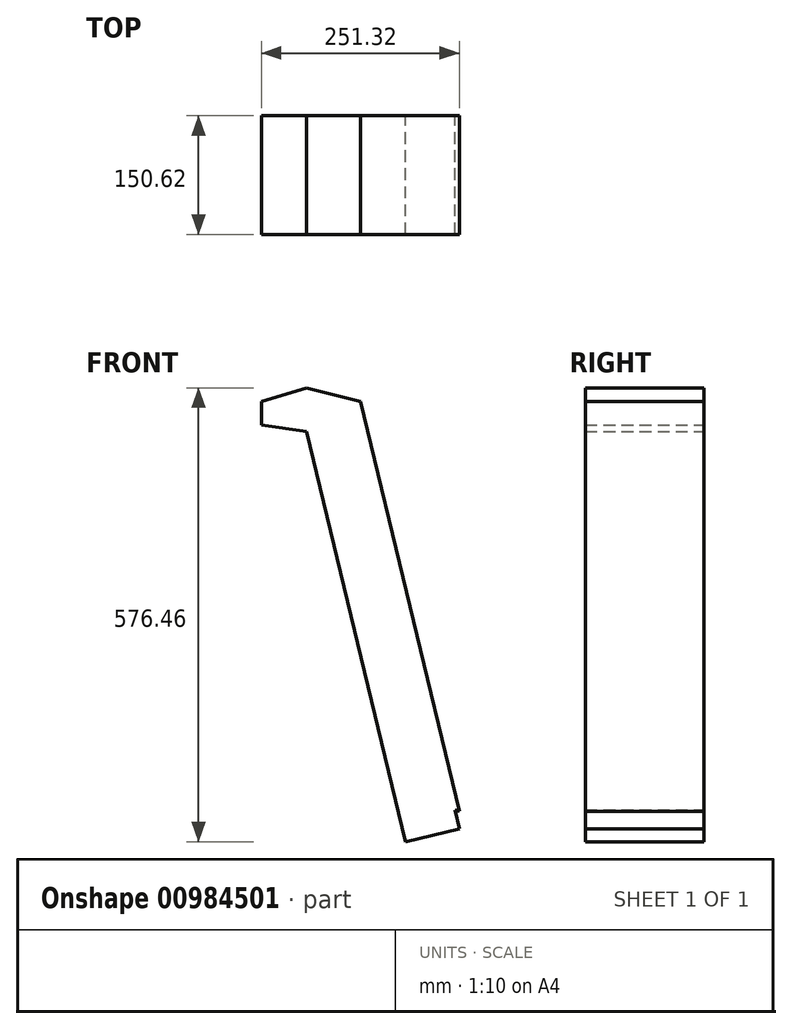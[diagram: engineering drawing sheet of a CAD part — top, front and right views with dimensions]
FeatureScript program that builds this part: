
annotation { "Feature Type Name" : "Feature", "Feature Type Description" : "" }
export const myFeature = defineFeature(function(context is Context, id is Id, definition is map)
    precondition{}
    {
        {
            var Q0;
            Q0=qCreatedBy(makeId("Front.planeOp"),FACE);
            var sketch = newSketch(context, id + "F0", { "sketchPlane" : qUnion([Q0])});
            skLineSegment(sketch, "E0", {"start": v(0, 0) * mm, "end": v(0, 55.7) * mm});
            skLineSegment(sketch, "E1", {"start": v(0, 55.7) * mm, "end": v(68.64, 38.7) * mm});
            skLineSegment(sketch, "E2", {"start": v(68.64, 38.7) * mm, "end": v(68.64, 16.55) * mm});
            skLineSegment(sketch, "E3", {"start": v(68.64, 16.55) * mm, "end": v(0, 0) * mm});
            skLineSegment(sketch, "E4", {"start": v(0, 0) * mm, "end": v(-57.13, 8.78) * mm});
            skLineSegment(sketch, "E5", {"start": v(-57.13, 8.78) * mm, "end": v(-57.13, 38.7) * mm});
            skLineSegment(sketch, "E6", {"start": v(-57.13, 38.7) * mm, "end": v(0, 55.7) * mm});
            skSolve(sketch);
        }
        {
            var Q0;
            Q0=makeQuery(id+"F0.imprint","IMPRINT",FACE,{"disambiguationData":[TD([[makeQuery(id+"F0.imprint","IMPRINT",EDGE,{"derivedFrom":sQuery(id+"F0.wireOp",EDGE,"E0")}),1.0]])]});
            var Q1;
            Q1=makeQuery(id+"F0.imprint","IMPRINT",FACE,{"disambiguationData":[TD([[makeQuery(id+"F0.imprint","IMPRINT",EDGE,{"derivedFrom":sQuery(id+"F0.wireOp",EDGE,"E0")}),-1.0]])]});
            extrude(context, id + "F1", {"entities" : qUnion([Q0, Q1]), "depth" : 150.62 * mm, "offsetDistance" : 25.4 * mm});
        }
        {
            var Q0;
            Q0=makeQuery(id+"F1.opExtrude","SWEPT_FACE",FACE,{"disambiguationData":[OSD([sQuery(id+"F0.wireOp",EDGE,"E3")])]});
            var Q1;
            Q1=makeQuery(id+"F1.opExtrude","SWEPT_FACE",FACE,{"disambiguationData":[OSD([sQuery(id+"F0.wireOp",EDGE,"E1")])]});
            extrude(context, id + "F2", {"entities" : qUnion([Q0, Q1]), "operationType" : NewBodyOperationType.ADD, "depth" : 535.7 * mm, "offsetDistance" : 25.4 * mm});
        }
    });
